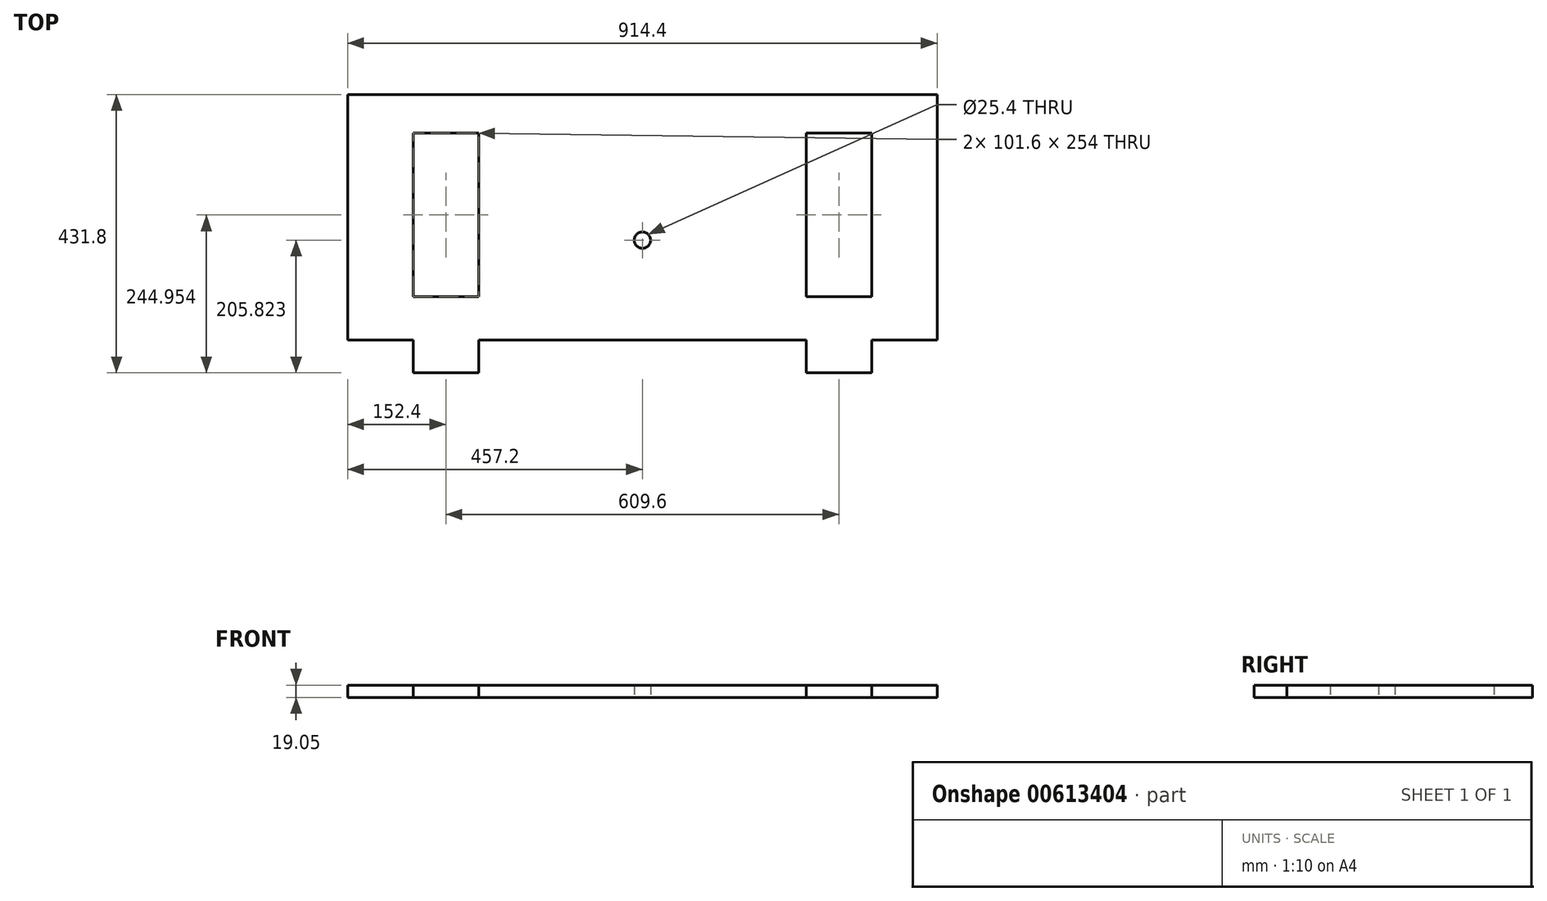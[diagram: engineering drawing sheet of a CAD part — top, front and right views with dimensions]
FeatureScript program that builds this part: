
annotation { "Feature Type Name" : "Feature", "Feature Type Description" : "" }
export const myFeature = defineFeature(function(context is Context, id is Id, definition is map)
    precondition{}
    {
        {
            var Q0;
            Q0=qCreatedBy(makeId("Top.planeOp"),FACE);
            var sketch = newSketch(context, id + "F0", { "sketchPlane" : qUnion([Q0])});
            skLineSegment(sketch, "E0.bottom", {"start": v(-457.2, 175.8) * mm, "end": v(457.2, 175.8) * mm});
            skLineSegment(sketch, "E0.top", {"start": v(-457.2, -205.2) * mm, "end": v(457.2, -205.2) * mm});
            skLineSegment(sketch, "E0.left", {"start": v(-457.2, 175.8) * mm, "end": v(-457.2, -205.2) * mm});
            skLineSegment(sketch, "E0.right", {"start": v(457.2, 175.8) * mm, "end": v(457.2, -205.2) * mm});
            skLineSegment(sketch, "E1", {"start": v(-355.6, 115.95) * mm, "end": v(-355.6, -138.05) * mm});
            skLineSegment(sketch, "E2", {"start": v(-254, -138.05) * mm, "end": v(-254, 115.95) * mm});
            skLineSegment(sketch, "E3", {"start": v(-355.6, -138.05) * mm, "end": v(-254, -138.05) * mm});
            skLineSegment(sketch, "E4", {"start": v(-355.6, 115.95) * mm, "end": v(-254, 115.95) * mm});
            skLineSegment(sketch, "E5", {"start": v(0, 175.8) * mm, "end": v(0, -205.2) * mm, "construction": true});
            skLineSegment(sketch, "E6.MirrorCS", {"start": v(254, -138.05) * mm, "end": v(254, 115.95) * mm});
            skLineSegment(sketch, "E7.MirrorCS", {"start": v(355.6, 115.95) * mm, "end": v(254, 115.95) * mm});
            skLineSegment(sketch, "E8.MirrorCS", {"start": v(355.6, 115.95) * mm, "end": v(355.6, -138.05) * mm});
            skLineSegment(sketch, "E9.MirrorCS", {"start": v(355.6, -138.05) * mm, "end": v(254, -138.05) * mm});
            skLineSegment(sketch, "E10", {"start": v(0, -205.2) * mm, "end": v(0, -50.18) * mm});
            skCircle(sketch, "E11", {"center": v(0, -50.18) * mm, "radius": 12.7 * mm});
            skLineSegment(sketch, "E12", {"start": v(-355.6, -205.2) * mm, "end": v(-355.6, -256) * mm});
            skLineSegment(sketch, "E13", {"start": v(-355.6, -256) * mm, "end": v(-254, -256) * mm});
            skLineSegment(sketch, "E14", {"start": v(-254, -205.2) * mm, "end": v(-254, -256) * mm});
            skLineSegment(sketch, "E15.MirrorCS", {"start": v(254, -205.2) * mm, "end": v(254, -256) * mm});
            skLineSegment(sketch, "E16.MirrorCS", {"start": v(355.6, -256) * mm, "end": v(254, -256) * mm});
            skLineSegment(sketch, "E17.MirrorCS", {"start": v(355.6, -205.2) * mm, "end": v(355.6, -256) * mm});
            skSolve(sketch);
        }
        {
            var Q0;
            Q0=qSketchRegion(id+"F0",true);
            extrude(context, id + "F1", {"entities" : qUnion([Q0]), "depth" : 19.05 * mm, "offsetDistance" : 25.4 * mm});
        }
    });
